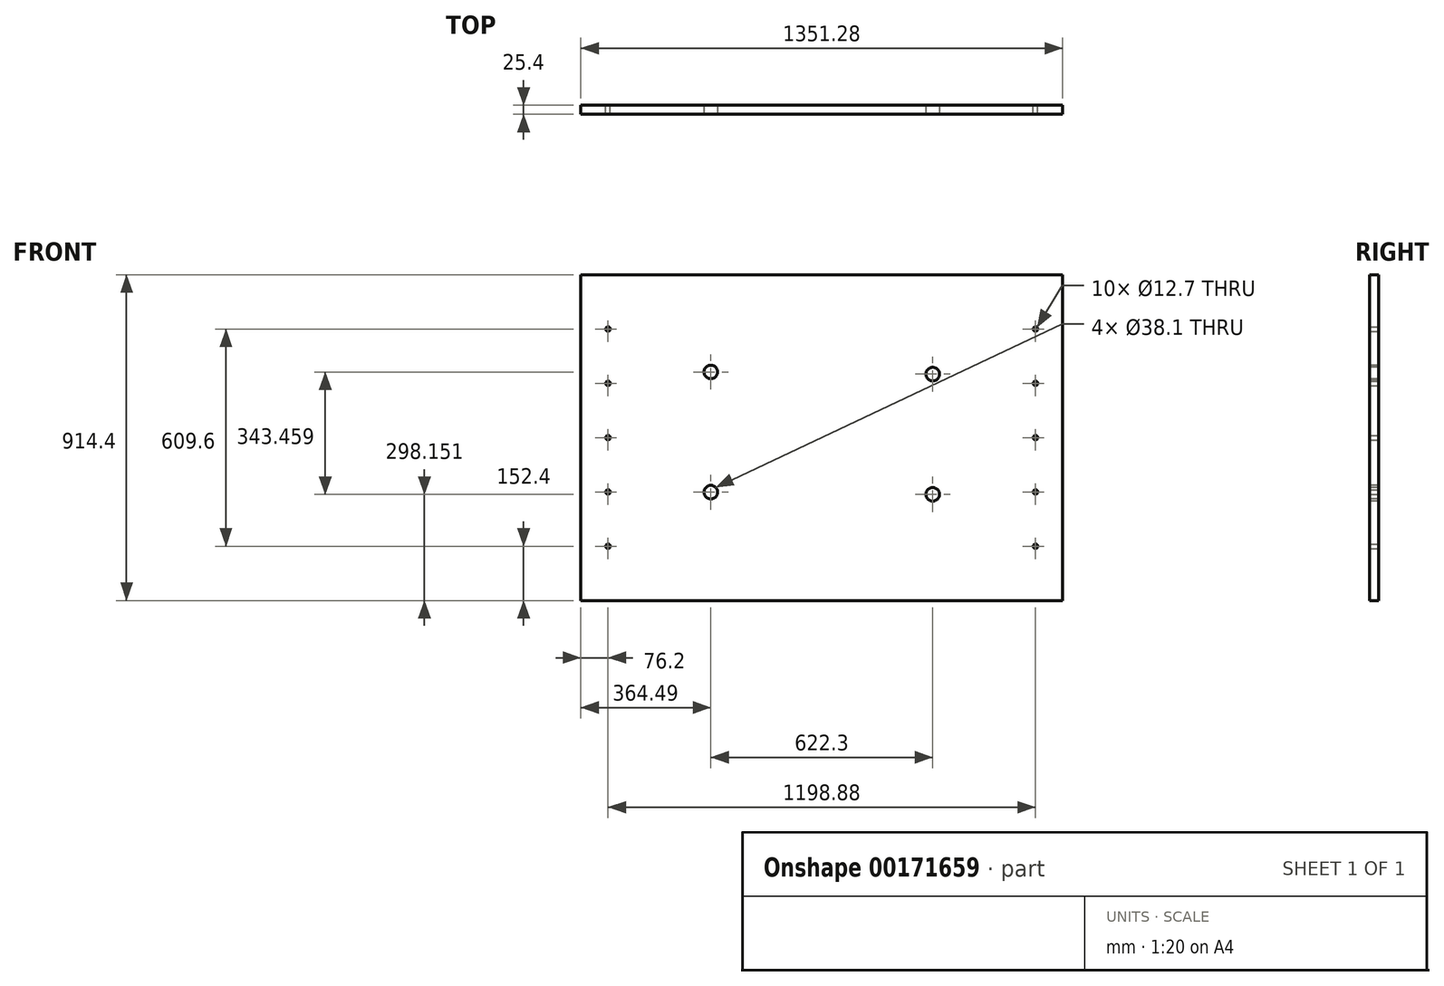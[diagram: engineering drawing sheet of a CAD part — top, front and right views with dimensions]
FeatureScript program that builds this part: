
annotation { "Feature Type Name" : "Feature", "Feature Type Description" : "" }
export const myFeature = defineFeature(function(context is Context, id is Id, definition is map)
    precondition{}
    {
        {
            var Q0;
            Q0=qCreatedBy(makeId("Front.planeOp"),FACE);
            var sketch = newSketch(context, id + "F0", { "sketchPlane" : qUnion([Q0])});
            skLineSegment(sketch, "E0.bottom", {"start": v(-675.64, 457.2) * mm, "end": v(675.64, 457.2) * mm});
            skLineSegment(sketch, "E0.top", {"start": v(-675.64, -457.2) * mm, "end": v(675.64, -457.2) * mm});
            skLineSegment(sketch, "E0.left", {"start": v(-675.64, 457.2) * mm, "end": v(-675.64, -457.2) * mm});
            skLineSegment(sketch, "E0.right", {"start": v(675.64, 457.2) * mm, "end": v(675.64, -457.2) * mm});
            skSolve(sketch);
        }
        {
            var Q0;
            Q0=makeQuery(id+"F0.imprint","IMPRINT",FACE,{"disambiguationData":[TD([[makeQuery(id+"F0.imprint","IMPRINT",EDGE,{"derivedFrom":sQuery(id+"F0.wireOp",EDGE,"E0.bottom")}),-1.0]])]});
            extrude(context, id + "F1", {"entities" : qUnion([Q0]), "depth" : 25.4 * mm});
        }
        {
            var Q0;
            Q0=makeQuery(id+"F1.opExtrude","CAP_FACE",FACE,{"disambiguationData":[OSD([sQuery(id+"F0.wireOp",EDGE,"E0.bottom"),sQuery(id+"F0.wireOp",EDGE,"E0.top"),sQuery(id+"F0.wireOp",EDGE,"E0.left"),sQuery(id+"F0.wireOp",EDGE,"E0.right")])],"isStart":false});
            var sketch = newSketch(context, id + "F2", { "sketchPlane" : qUnion([Q0])});
            skCircle(sketch, "E1", {"center": v(-599.44, 304.8) * mm, "radius": 6.35 * mm});
            skCircle(sketch, "E2", {"center": v(-599.44, 152.4) * mm, "radius": 6.35 * mm});
            skCircle(sketch, "E3", {"center": v(-599.44, 0) * mm, "radius": 6.35 * mm});
            skCircle(sketch, "E4", {"center": v(-599.44, -152.4) * mm, "radius": 6.35 * mm});
            skCircle(sketch, "E5", {"center": v(-599.44, -304.8) * mm, "radius": 6.35 * mm});
            skCircle(sketch, "E6.MirrorC", {"center": v(599.44, -304.8) * mm, "radius": 6.35 * mm});
            skCircle(sketch, "E7.MirrorC", {"center": v(599.44, 0) * mm, "radius": 6.35 * mm});
            skCircle(sketch, "E8.MirrorC", {"center": v(599.44, 304.8) * mm, "radius": 6.35 * mm});
            skCircle(sketch, "E9.MirrorC", {"center": v(599.44, 152.4) * mm, "radius": 6.35 * mm});
            skCircle(sketch, "E10.MirrorC", {"center": v(599.44, -152.4) * mm, "radius": 6.35 * mm});
            skSolve(sketch);
        }
        {
            var Q0;
            Q0=sQuery(id+"F2.wireOp",VERTEX,"E4.center");
            var Q1;
            Q1=sQuery(id+"F2.wireOp",VERTEX,"E3.center");
            var Q2;
            Q2=sQuery(id+"F2.wireOp",VERTEX,"E2.center");
            var Q3;
            Q3=sQuery(id+"F2.wireOp",VERTEX,"E1.center");
            var Q4;
            Q4=sQuery(id+"F2.wireOp",VERTEX,"E5.center");
            var Q5;
            Q5=sQuery(id+"F2.wireOp",VERTEX,"E8.MirrorC.center");
            var Q6;
            Q6=sQuery(id+"F2.wireOp",VERTEX,"E9.MirrorC.center");
            var Q7;
            Q7=sQuery(id+"F2.wireOp",VERTEX,"E7.MirrorC.center");
            var Q8;
            Q8=sQuery(id+"F2.wireOp",VERTEX,"E10.MirrorC.center");
            var Q9;
            Q9=sQuery(id+"F2.wireOp",VERTEX,"E6.MirrorC.center");
            var Q10;
            Q10=makeQuery(id+"F1.opExtrude","SWEPT_BODY",BODY,{"disambiguationData":[OSD([sQuery(id+"F0.wireOp",EDGE,"E0.bottom"),sQuery(id+"F0.wireOp",EDGE,"E0.top"),sQuery(id+"F0.wireOp",EDGE,"E0.left"),sQuery(id+"F0.wireOp",EDGE,"E0.right")])]});
            hole(context, id + "F3", {"style" : HoleStyle.SIMPLE, "endStyle" : HoleEndStyle.THROUGH, "holeDiameter" : 12.7 * mm, "locations" : qUnion([Q0, Q1, Q2, Q3, Q4, Q5, Q6, Q7, Q8, Q9]), "scope" : qUnion([Q10]), "isTappedThrough" : true});
        }
        {
            var Q0;
            Q0=makeQuery(id+"F1.opExtrude","CAP_FACE",FACE,{"disambiguationData":[OSD([sQuery(id+"F0.wireOp",EDGE,"E0.bottom"),sQuery(id+"F0.wireOp",EDGE,"E0.top"),sQuery(id+"F0.wireOp",EDGE,"E0.left"),sQuery(id+"F0.wireOp",EDGE,"E0.right")])],"isStart":false});
            var sketch = newSketch(context, id + "F4", { "sketchPlane" : qUnion([Q0])});
            skPoint(sketch, "E11", {"position": v(-311.15, 184.4) * mm});
            skPoint(sketch, "E12", {"position": v(311.15, 178.26) * mm});
            skPoint(sketch, "E13", {"position": v(-311.15, -152.9) * mm});
            skPoint(sketch, "E14", {"position": v(311.15, -159.05) * mm});
            skPoint(sketch, "E15", {"position": v(-675.64, 457.2) * mm});
            skPoint(sketch, "E16", {"position": v(675.64, 457.2) * mm});
            skCircle(sketch, "E17", {"center": v(-311.15, 184.4) * mm, "radius": 19.05 * mm});
            skCircle(sketch, "E18", {"center": v(-311.15, -152.9) * mm, "radius": 19.05 * mm});
            skCircle(sketch, "E19", {"center": v(311.15, 178.26) * mm, "radius": 19.05 * mm});
            skCircle(sketch, "E20", {"center": v(311.15, -159.05) * mm, "radius": 19.05 * mm});
            skSolve(sketch);
        }
        {
            var Q0;
            Q0=makeQuery(id+"F4.imprint","IMPRINT",FACE,{"disambiguationData":[TD([[makeQuery(id+"F4.imprint","IMPRINT",EDGE,{"derivedFrom":sQuery(id+"F4.wireOp",EDGE,"E17")}),1.0]])]});
            var Q1;
            Q1=makeQuery(id+"F4.imprint","IMPRINT",FACE,{"disambiguationData":[TD([[makeQuery(id+"F4.imprint","IMPRINT",EDGE,{"derivedFrom":sQuery(id+"F4.wireOp",EDGE,"E18")}),1.0]])]});
            var Q2;
            Q2=makeQuery(id+"F4.imprint","IMPRINT",FACE,{"disambiguationData":[TD([[makeQuery(id+"F4.imprint","IMPRINT",EDGE,{"derivedFrom":sQuery(id+"F4.wireOp",EDGE,"E20")}),1.0]])]});
            var Q3;
            Q3=makeQuery(id+"F4.imprint","IMPRINT",FACE,{"disambiguationData":[TD([[makeQuery(id+"F4.imprint","IMPRINT",EDGE,{"derivedFrom":sQuery(id+"F4.wireOp",EDGE,"E19")}),1.0]])]});
            extrude(context, id + "F5", {"entities" : qUnion([Q0, Q1, Q2, Q3]), "operationType" : NewBodyOperationType.REMOVE, "oppositeDirection" : true, "depth" : 127 * mm});
        }
    });
